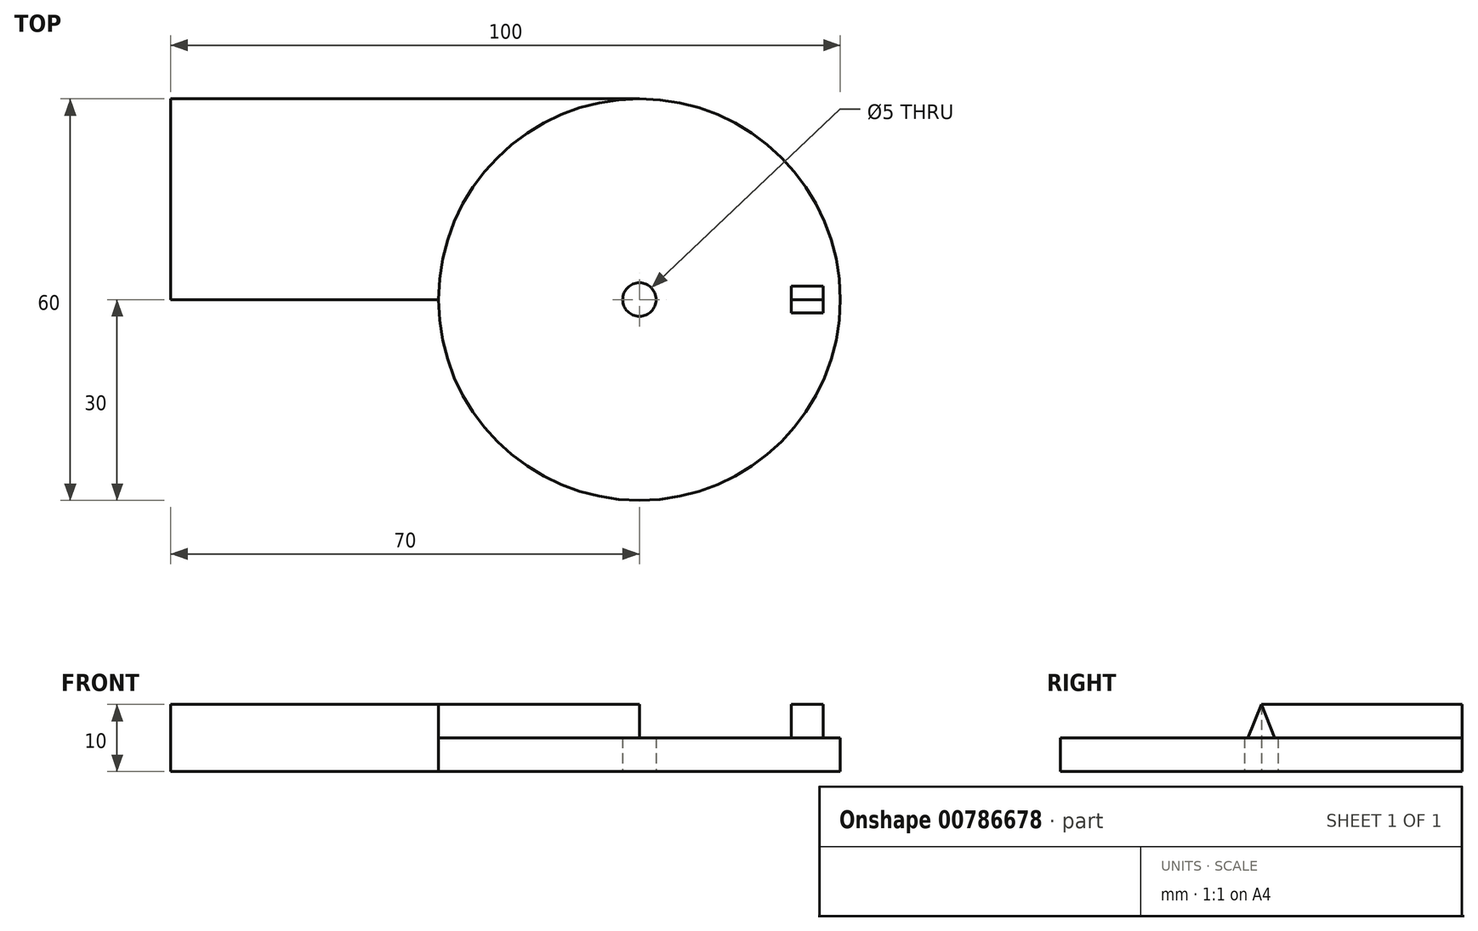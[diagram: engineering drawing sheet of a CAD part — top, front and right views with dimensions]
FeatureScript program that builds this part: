
annotation { "Feature Type Name" : "Feature", "Feature Type Description" : "" }
export const myFeature = defineFeature(function(context is Context, id is Id, definition is map)
    precondition{}
    {
        {
            var Q0;
            Q0=qCreatedBy(makeId("Top.planeOp"),FACE);
            var sketch = newSketch(context, id + "F0", { "sketchPlane" : qUnion([Q0])});
            skLineSegment(sketch, "E0.bottom", {"start": v(35, -15) * mm, "end": v(-35, -15) * mm});
            skLineSegment(sketch, "E0.top", {"start": v(35, 15) * mm, "end": v(-35, 15) * mm});
            skLineSegment(sketch, "E0.left", {"start": v(35, -15) * mm, "end": v(35, 15) * mm});
            skLineSegment(sketch, "E0.right", {"start": v(-35, -15) * mm, "end": v(-35, 15) * mm});
            skPoint(sketch, "E0.middle", {"position": v(0, 0) * mm});
            skCircle(sketch, "E1", {"center": v(35, -15) * mm, "radius": 30 * mm});
            skCircle(sketch, "E2", {"center": v(35, -15) * mm, "radius": 2.5 * mm});
            skCircle(sketch, "E3", {"center": v(35, -15) * mm, "radius": 27.5 * mm});
            skCircle(sketch, "E4", {"center": v(35, -15) * mm, "radius": 22.5 * mm});
            skSolve(sketch);
        }
        {
            var Q0;
            {var subQ4=sQuery(id+"F0.wireOp",EDGE,"E0.top");Q0=makeQuery(id+"F0.imprint","IMPRINT",FACE,{"disambiguationData":[TD([[makeQuery(id+"F0.imprint","IMPRINT",EDGE,{"derivedFrom":subQ4}),1.0]])]});}
            extrude(context, id + "F1", {"entities" : qUnion([Q0]), "depth" : 10 * mm, "offsetDistance" : 25 * mm});
        }
        {
            var Q0;
            {var subQ0=sQuery(id+"F0.wireOp",EDGE,"E1");var subQ1=sQuery(id+"F0.wireOp",EDGE,"E0.bottom");var subQ2=makeQuery(id+"F0.imprint","INTERSECT",VERTEX,{"derivedFrom":[subQ1,subQ0]});Q0=makeQuery(id+"F0.imprint","IMPRINT",FACE,{"disambiguationData":[TD([[makeQuery(id+"F0.imprint","IMPRINT",EDGE,{"disambiguationData":[TD([[subQ2,1.0]])],"derivedFrom":subQ1}),-1.0]])]});}
            var Q1;
            {var subQ0=sQuery(id+"F0.wireOp",EDGE,"E4");var subQ1=sQuery(id+"F0.wireOp",EDGE,"E0.bottom");var subQ2=makeQuery(id+"F0.imprint","INTERSECT",VERTEX,{"derivedFrom":[subQ1,subQ0]});Q1=makeQuery(id+"F0.imprint","IMPRINT",FACE,{"disambiguationData":[TD([[makeQuery(id+"F0.imprint","IMPRINT",EDGE,{"disambiguationData":[TD([[subQ2,-1.0]])],"derivedFrom":subQ1}),-1.0]])]});}
            var Q2;
            {var subQ0=sQuery(id+"F0.wireOp",EDGE,"E1");var subQ1=sQuery(id+"F0.wireOp",EDGE,"E0.bottom");var subQ2=makeQuery(id+"F0.imprint","INTERSECT",VERTEX,{"derivedFrom":[subQ1,subQ0]});Q2=makeQuery(id+"F0.imprint","IMPRINT",FACE,{"disambiguationData":[TD([[makeQuery(id+"F0.imprint","IMPRINT",EDGE,{"disambiguationData":[TD([[subQ2,1.0]])],"derivedFrom":subQ1}),1.0]])]});}
            var Q3;
            {var subQ0=sQuery(id+"F0.wireOp",EDGE,"E4");var subQ1=sQuery(id+"F0.wireOp",EDGE,"E0.bottom");var subQ2=makeQuery(id+"F0.imprint","INTERSECT",VERTEX,{"derivedFrom":[subQ1,subQ0]});Q3=makeQuery(id+"F0.imprint","IMPRINT",FACE,{"disambiguationData":[TD([[makeQuery(id+"F0.imprint","IMPRINT",EDGE,{"disambiguationData":[TD([[subQ2,-1.0]])],"derivedFrom":subQ1}),1.0]])]});}
            var Q4;
            {var subQ0=sQuery(id+"F0.wireOp",EDGE,"E2");var subQ1=sQuery(id+"F0.wireOp",EDGE,"E0.bottom");var subQ2=makeQuery(id+"F0.imprint","INTERSECT",VERTEX,{"derivedFrom":[subQ1,subQ0]});Q4=makeQuery(id+"F0.imprint","IMPRINT",FACE,{"disambiguationData":[TD([[makeQuery(id+"F0.imprint","IMPRINT",EDGE,{"disambiguationData":[TD([[subQ2,-1.0]])],"derivedFrom":subQ1}),-1.0]])]});}
            var Q5;
            {var subQ0=sQuery(id+"F0.wireOp",EDGE,"E2");var subQ1=sQuery(id+"F0.wireOp",EDGE,"E0.bottom");var subQ2=makeQuery(id+"F0.imprint","INTERSECT",VERTEX,{"derivedFrom":[subQ1,subQ0]});Q5=makeQuery(id+"F0.imprint","IMPRINT",FACE,{"disambiguationData":[TD([[makeQuery(id+"F0.imprint","IMPRINT",EDGE,{"disambiguationData":[TD([[subQ2,-1.0]])],"derivedFrom":subQ1}),1.0]])]});}
            extrude(context, id + "F2", {"entities" : qUnion([Q0, Q1, Q2, Q3, Q4, Q5]), "operationType" : NewBodyOperationType.ADD, "depth" : 5 * mm, "offsetDistance" : 25 * mm});
        }
        {
            var Q0;
            Q0=makeQuery(id+"F2.opExtrude","CAP_FACE",FACE,{"disambiguationData":[OSD([sQuery(id+"F0.wireOp",EDGE,"E1"),sQuery(id+"F0.wireOp",EDGE,"E2")])],"isStart":false});
            var sketch = newSketch(context, id + "F3", { "sketchPlane" : qUnion([Q0])});
            skLineSegment(sketch, "E5", {"start": v(35, -15) * mm, "end": v(65, -15) * mm});
            skCircle(sketch, "E6", {"center": v(35, -15) * mm, "radius": 22.5 * mm});
            skCircle(sketch, "E7", {"center": v(35, -15) * mm, "radius": 27.5 * mm});
            skLineSegment(sketch, "E8", {"start": v(57.41, -13) * mm, "end": v(62.43, -13) * mm});
            skLineSegment(sketch, "E9", {"start": v(57.41, -17) * mm, "end": v(62.43, -17) * mm});
            skLineSegment(sketch, "E10", {"start": v(57.5, -13) * mm, "end": v(57.5, -17) * mm});
            skLineSegment(sketch, "E11", {"start": v(62.43, -13) * mm, "end": v(62.43, -17) * mm});
            skSolve(sketch);
        }
        {
            var Q0;
            {var subQ0=sQuery(id+"F3.wireOp",EDGE,"E11");var subQ1=sQuery(id+"F3.wireOp",EDGE,"E5");var subQ2=makeQuery(id+"F3.imprint","INTERSECT",VERTEX,{"derivedFrom":[subQ1,subQ0]});Q0=makeQuery(id+"F3.imprint","IMPRINT",FACE,{"disambiguationData":[TD([[makeQuery(id+"F3.imprint","IMPRINT",EDGE,{"disambiguationData":[TD([[subQ2,1.0]])],"derivedFrom":subQ1}),1.0]])]});}
            var Q1;
            {var subQ0=sQuery(id+"F3.wireOp",EDGE,"E11");var subQ1=sQuery(id+"F3.wireOp",EDGE,"E5");var subQ2=makeQuery(id+"F3.imprint","INTERSECT",VERTEX,{"derivedFrom":[subQ1,subQ0]});Q1=makeQuery(id+"F3.imprint","IMPRINT",FACE,{"disambiguationData":[TD([[makeQuery(id+"F3.imprint","IMPRINT",EDGE,{"disambiguationData":[TD([[subQ2,1.0]])],"derivedFrom":subQ1}),-1.0]])]});}
            var Q2;
            Q2=makeQuery(id+"F1.opExtrude","CAP_FACE",FACE,{"disambiguationData":[OSD([sQuery(id+"F0.wireOp",EDGE,"E0.bottom"),sQuery(id+"F0.wireOp",EDGE,"E0.top"),sQuery(id+"F0.wireOp",EDGE,"E0.right"),sQuery(id+"F0.wireOp",EDGE,"E1")])],"isStart":false});
            extrude(context, id + "F4", {"entities" : qUnion([Q0, Q1]), "operationType" : NewBodyOperationType.ADD, "endBound" : BoundingType.UP_TO_SURFACE, "depth" : 2.5 * mm, "endBoundEntityFace" : qUnion([Q2]), "offsetDistance" : 25 * mm});
        }
        {
            var Q0;
            Q0=makeQuery(id+"F4.opExtrude","SWEPT_FACE",FACE,{"disambiguationData":[OSD([sQuery(id+"F3.wireOp",EDGE,"E11")])]});
            var sketch = newSketch(context, id + "F5", { "sketchPlane" : qUnion([Q0])});
            skLineSegment(sketch, "E12", {"start": v(-17, 5) * mm, "end": v(-15, 10) * mm});
            skLineSegment(sketch, "E13", {"start": v(-15, 10) * mm, "end": v(-13, 5) * mm});
            skLineSegment(sketch, "E14", {"start": v(-13, 5) * mm, "end": v(-17, 5) * mm});
            skSolve(sketch);
        }
        {
            var Q0;
            {var subQ0=sQuery(id+"F5.wireOp",EDGE,"E12");Q0=makeQuery(id+"F5.imprint","IMPRINT",FACE,{"disambiguationData":[TD([[makeQuery(id+"F5.imprint","IMPRINT",EDGE,{"derivedFrom":subQ0}),1.0]])]});}
            var Q1;
            {var subQ0=sQuery(id+"F5.wireOp",EDGE,"E13");Q1=makeQuery(id+"F5.imprint","IMPRINT",FACE,{"disambiguationData":[TD([[makeQuery(id+"F5.imprint","IMPRINT",EDGE,{"derivedFrom":subQ0}),1.0]])]});}
            var Q2;
            Q2=makeQuery(id+"F4.opExtrude","SWEPT_FACE",FACE,{"disambiguationData":[OSD([sQuery(id+"F3.wireOp",EDGE,"E10")])]});
            extrude(context, id + "F6", {"entities" : qUnion([Q0, Q1]), "operationType" : NewBodyOperationType.REMOVE, "endBound" : BoundingType.UP_TO_SURFACE, "oppositeDirection" : true, "depth" : 25 * mm, "endBoundEntityFace" : qUnion([Q2]), "offsetDistance" : 25 * mm});
        }
        {
            var Q0;
            Q0=makeQuery(id+"F4.opExtrude","SWEPT_FACE",FACE,{"disambiguationData":[OSD([sQuery(id+"F3.wireOp",EDGE,"E11")])]});
            extrude(context, id + "F7", {"entities" : qUnion([Q0]), "operationType" : NewBodyOperationType.REMOVE, "oppositeDirection" : true, "depth" : -0.2 * mm, "offsetDistance" : 25 * mm});
        }
        {
            var Q0;
            Q0=makeQuery(id+"F4.opExtrude","SWEPT_FACE",FACE,{"disambiguationData":[OSD([sQuery(id+"F3.wireOp",EDGE,"E10")])]});
            extrude(context, id + "F8", {"entities" : qUnion([Q0]), "operationType" : NewBodyOperationType.REMOVE, "oppositeDirection" : true, "depth" : 0.2 * mm, "offsetDistance" : 25 * mm});
        }
    });
